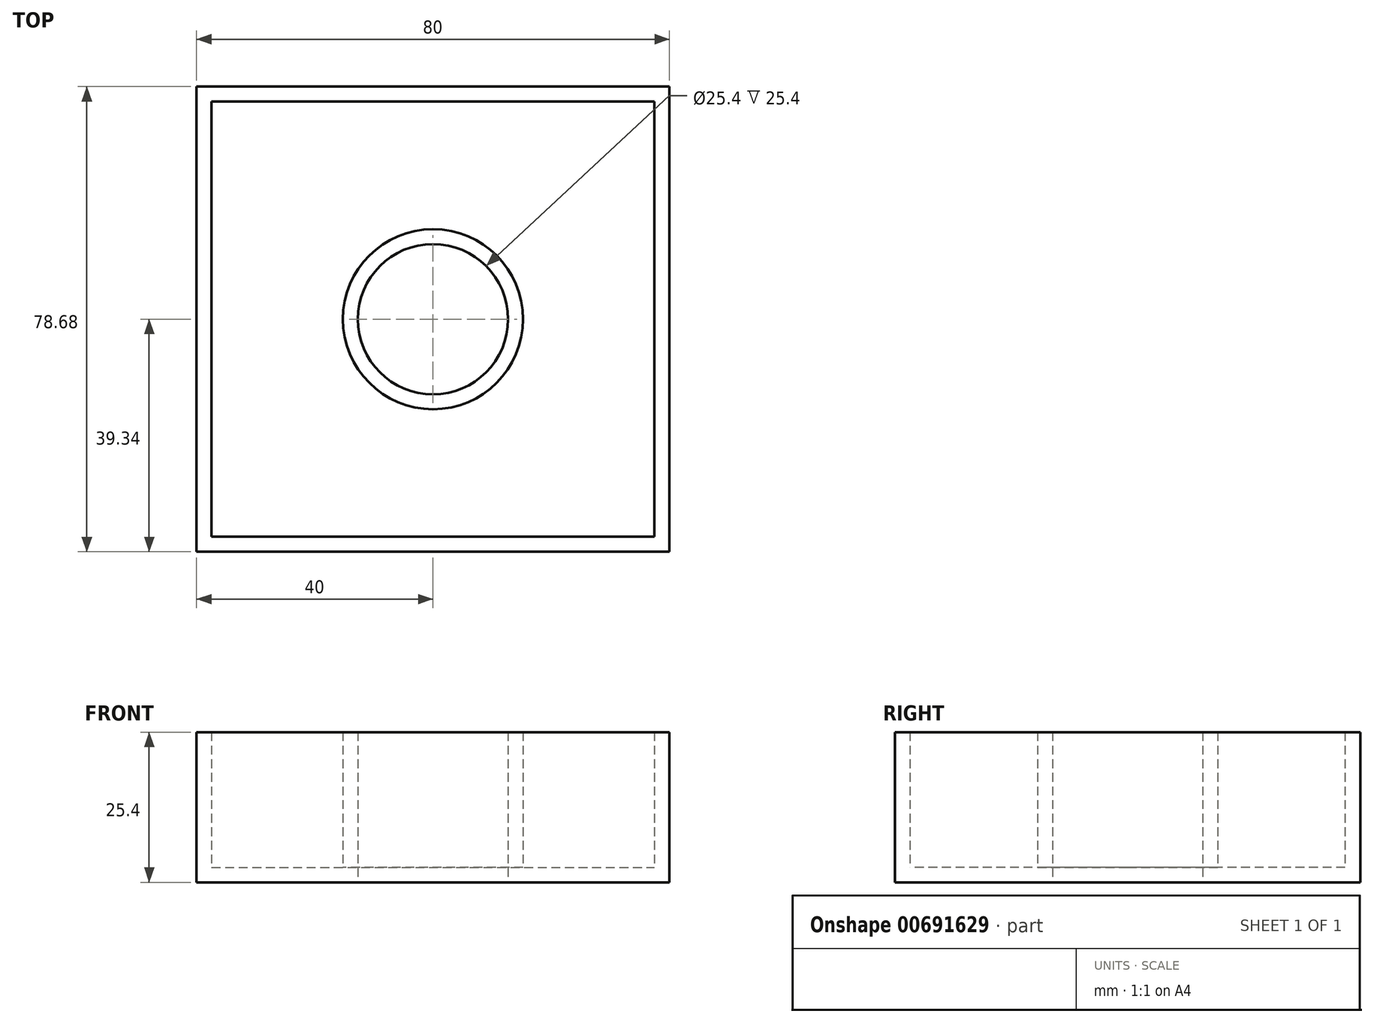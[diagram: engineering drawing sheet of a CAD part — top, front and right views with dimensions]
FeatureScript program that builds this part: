
annotation { "Feature Type Name" : "Feature", "Feature Type Description" : "" }
export const myFeature = defineFeature(function(context is Context, id is Id, definition is map)
    precondition{}
    {
        {
            var Q0;
            Q0=qCreatedBy(makeId("Top.planeOp"),FACE);
            var sketch = newSketch(context, id + "F0", { "sketchPlane" : qUnion([Q0])});
            skLineSegment(sketch, "E0.bottom", {"start": v(-40, 39.34) * mm, "end": v(40, 39.34) * mm});
            skLineSegment(sketch, "E0.top", {"start": v(-40, -39.34) * mm, "end": v(40, -39.34) * mm});
            skLineSegment(sketch, "E0.left", {"start": v(-40, 39.34) * mm, "end": v(-40, -39.34) * mm});
            skLineSegment(sketch, "E0.right", {"start": v(40, 39.34) * mm, "end": v(40, -39.34) * mm});
            skSolve(sketch);
        }
        {
            var Q0;
            Q0=makeQuery(id+"F0.imprint","IMPRINT",FACE,{"disambiguationData":[TD([[makeQuery(id+"F0.imprint","IMPRINT",EDGE,{"derivedFrom":sQuery(id+"F0.wireOp",EDGE,"E0.bottom")}),-1.0]])]});
            var sketch = newSketch(context, id + "F1", { "sketchPlane" : qUnion([Q0])});
            skCircle(sketch, "E1", {"center": v(0, 0) * mm, "radius": 12.7 * mm});
            skSolve(sketch);
        }
        {
            var Q0;
            Q0=makeQuery(id+"F1.imprint","IMPRINT",FACE,{"disambiguationData":[TD([[makeQuery(id+"F1.imprint","IMPRINT",EDGE,{"derivedFrom":sQuery(id+"F1.wireOp",EDGE,"E1")}),-1.0]])]});
            extrude(context, id + "F2", {"entities" : qUnion([Q0]), "depth" : 25.4 * mm, "offsetDistance" : 25.4 * mm});
        }
        {
            var Q0;
            Q0=makeQuery(id+"F2.opExtrude","CAP_FACE",FACE,{"disambiguationData":[OSD([sQuery(id+"F0.wireOp",EDGE,"E0.bottom"),sQuery(id+"F0.wireOp",EDGE,"E0.top"),sQuery(id+"F0.wireOp",EDGE,"E0.left"),sQuery(id+"F0.wireOp",EDGE,"E0.right"),sQuery(id+"F1.wireOp",EDGE,"E1")])],"isStart":false});
            shell(context, id + "F3", {"entities" : qUnion([Q0]), "thickness" : 2.54 * mm});
        }
    });
